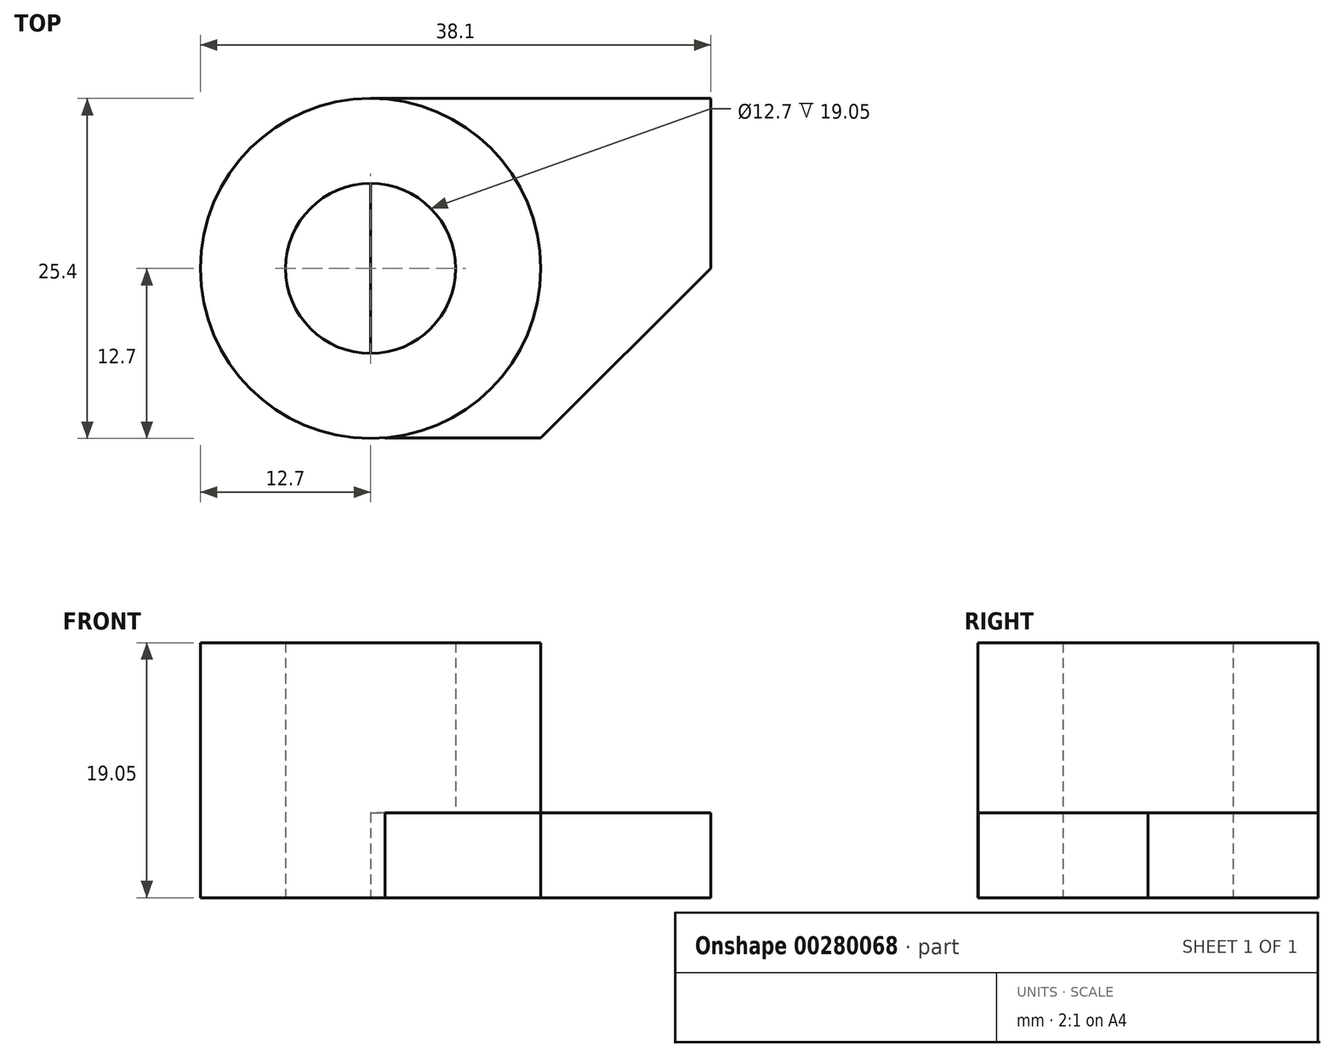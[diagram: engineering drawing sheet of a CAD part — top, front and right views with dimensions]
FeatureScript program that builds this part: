
annotation { "Feature Type Name" : "Feature", "Feature Type Description" : "" }
export const myFeature = defineFeature(function(context is Context, id is Id, definition is map)
    precondition{}
    {
        {
            var Q0;
            Q0=qCreatedBy(makeId("Top.planeOp"),FACE);
            var sketch = newSketch(context, id + "F0", { "sketchPlane" : qUnion([Q0])});
            skCircle(sketch, "E0", {"center": v(0, 0) * mm, "radius": 6.35 * mm});
            skCircle(sketch, "E1", {"center": v(0, 0) * mm, "radius": 12.7 * mm});
            skSolve(sketch);
        }
        {
            var Q0;
            Q0 = qSketchRegion(id + "F0", true);
            extrude(context, id + "F1", {"entities" : qUnion([Q0]), "depth" : 19.05 * mm});
        }
        {
            var Q0;
            Q0=qCreatedBy(makeId("Top.planeOp"),FACE);
            var sketch = newSketch(context, id + "F2", { "sketchPlane" : qUnion([Q0])});
            skPoint(sketch, "E2.middle", {"position": v(-12.76, 0) * mm});
            skLineSegment(sketch, "E3", {"start": v(0, 12.7) * mm, "end": v(25.4, 12.7) * mm});
            skLineSegment(sketch, "E4", {"start": v(25.4, 12.7) * mm, "end": v(25.4, 0) * mm});
            skLineSegment(sketch, "E5", {"start": v(0, -12.66) * mm, "end": v(12.7, -12.66) * mm});
            skLineSegment(sketch, "E6", {"start": v(25.4, 0) * mm, "end": v(12.7, -12.66) * mm});
            skLineSegment(sketch, "E7", {"start": v(0, 12.7) * mm, "end": v(0, -12.66) * mm});
            skSolve(sketch);
        }
        {
            var Q0;
            Q0 = qSketchRegion(id + "F2", true);
            extrude(context, id + "F3", {"entities" : qUnion([Q0]), "operationType" : NewBodyOperationType.ADD, "depth" : 6.35 * mm});
        }
    });
